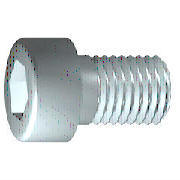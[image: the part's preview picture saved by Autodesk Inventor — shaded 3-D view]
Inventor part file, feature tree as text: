
AUTODESK INVENTOR PART (.ipt)
format: ipt  version: 2017 (Build 210142000, 142)  size: 188,928 bytes
history: native  units: mm (DEFAULTED — no unit token found)
features: sketch x2, extrude x1, plane x1, fillet x1
ambient origin geometry x7: Origin, YZ Plane, XY Plane, X Axis, Y Axis, Z Axis, Center Point
bodies: Solid1 (feature_tree), Body (feature_tree)
feature tree (5):
  extrude  "Slot"  Depth=5.0mm
  plane  "Work Plane1"
  fillet  "Fillet2"  Radius=5.0mm
  sketch  "Sketch1"  dims[d1=23.51848mm d2=0.49086mm d3=5.0mm]
  sketch  "Sketch2"  dims[d4=2.5mm d5=60.0deg d6=5.0mm d7=5.0mm d8=4.618802mm d9=8.5mm d10=90.0deg d11=10.0mm d12=0.0mm d13=23.51848mm d14=0.0mm d15=0.49076mm d16=0.49076mm d17=0.5mm d19=0.0mm d26=25.0mm d27=45.0deg d28=0.0mm d29=0.0mm d30=0.1mm]
